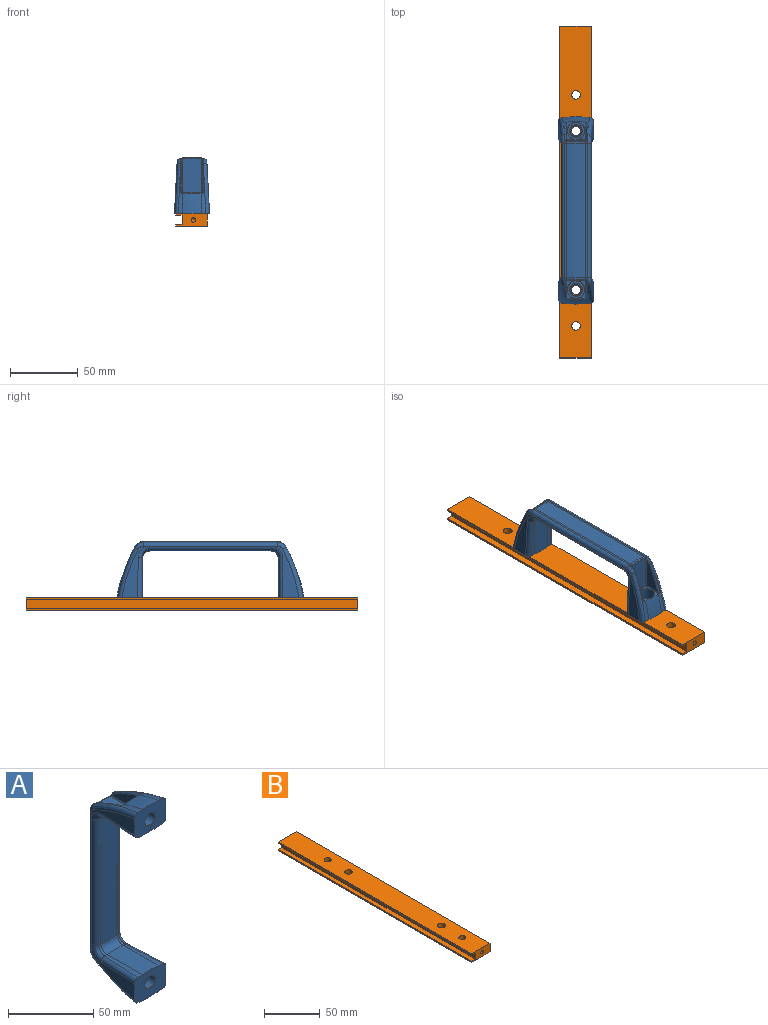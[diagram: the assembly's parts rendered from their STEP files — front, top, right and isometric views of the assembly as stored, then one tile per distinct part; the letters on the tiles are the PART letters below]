
ASSEMBLY  parts=2 mates=1
PART A: 126 faces, bbox 108.4x66.4x148.5 mm
  f0: bspline ~10.41x1.42mm, area 0.9mm2, adj f1,f4,f12,f108,f116
  f1: bspline ~20.12x1.18mm, area 9.2mm2, adj f0,f2,f15,f108
  f2: bspline ~9.59x1.35mm, area 0.9mm2, adj f1,f3,f13,f108,f112
  f3: bspline ~1.58x0.7mm, area 0.1mm2, adj f2,f53,f111
  f4: bspline ~1.56x0.73mm, area 0.1mm2, adj f0,f61,f113
  f5: bspline ~12.79x7.19mm, area 9.4mm2, adj f6,f7,f52,f110
  f6: torus R=125.24mm, axis (1,0,0), area 29.9mm2, adj f5,f14,f110,f115
  f7: bspline ~7.07x5.88mm, area 9.7mm2, adj f5,f53,f110,f111,f112,f114
  f8: bspline ~12.79x7.19mm, area 9.4mm2, adj f9,f10,f60,f107
  f9: torus R=125.24mm, axis (-1,0,0), area 29.9mm2, adj f8,f11,f107,f125
  f10: bspline ~7.07x5.88mm, area 9.7mm2, adj f8,f61,f107,f113,f116,f119
  f11: cone r=127mm half-angle=5deg, axis (-1,0,0), area 57.6mm2, adj f9,f29,f60,f75,f109,f125
  f12: cone r=7.92mm half-angle=5deg, axis (-1,0,0), area 2.4mm2, adj f0,f15,f41,f61
  f13: cone r=7.92mm half-angle=5deg, axis (1,0,0), area 2.4mm2, adj f2,f15,f46,f53
  f14: cone r=127mm half-angle=5deg, axis (1,0,0), area 57.6mm2, adj f6,f29,f52,f75,f109,f115
  f15: revolved ~13.28x1.56mm, area 20.6mm2, adj f1,f12,f13,f74
  f16: bspline ~10.41x1.42mm, area 0.9mm2, adj f17,f20,f45,f83,f87
  f17: bspline ~20.12x1.18mm, area 9.2mm2, adj f16,f18,f73,f83
  f18: bspline ~9.59x1.35mm, area 0.9mm2, adj f17,f19,f42,f83,f93
  f19: bspline ~1.56x0.73mm, area 0.1mm2, adj f18,f58,f90
  f20: bspline ~1.58x0.7mm, area 0.1mm2, adj f16,f55,f86
  f21: bspline ~12.79x7.19mm, area 9.4mm2, adj f22,f23,f57,f82
  f22: bspline ~7.07x5.88mm, area 9.7mm2, adj f21,f58,f82,f90,f93,f95
  f23: torus R=125.24mm, axis (1,0,0), area 29.9mm2, adj f21,f43,f82,f100
  f24: bspline ~12.79x7.19mm, area 9.4mm2, adj f25,f26,f56,f85
  f25: torus R=125.24mm, axis (-1,0,0), area 29.9mm2, adj f24,f44,f85,f88
  f26: bspline ~7.07x5.88mm, area 9.7mm2, adj f24,f55,f85,f86,f87,f89
  f27: plane 130.63x37.88mm, normal (1,0.05,0), area 541.9mm2, adj f28,f29,f57,f58,f59,f60,f61,f62
  f28: plane 26.01x19.26mm, normal (0,-1,0), area 410.5mm2, adj f27,f30,f31,f36,f43,f44,f47,f56
  f29: plane 26.01x19.26mm, normal (0,-1,0), area 410.5mm2, adj f11,f14,f27,f30,f34,f37,f51,f52
  f30: plane 130.63x37.88mm, normal (-1,0.05,0), area 541.9mm2, adj f28,f29,f47,f48,f49,f50,f51,f52
  f31: plane 29.17x3.53mm, normal (-0.09,0,-1), area 80.9mm2, adj f28,f35,f47,f71
  f32: plane 89.92x1.56mm, normal (-0.09,-1,0), area 140.9mm2, adj f33,f35,f49,f69
  f33: cone r=4.57mm half-angle=5deg, axis (-1,0,0), area 14.7mm2, adj f32,f34,f50,f68
  f34: plane 29.17x3.53mm, normal (-0.09,0,1), area 80.9mm2, adj f29,f33,f51,f67
  f35: cone r=4.57mm half-angle=5deg, axis (-1,0,0), area 14.7mm2, adj f31,f32,f48,f70
  f36: plane 29.17x3.53mm, normal (0.09,0,-1), area 80.9mm2, adj f28,f40,f62,f71
  f37: plane 29.17x3.53mm, normal (0.09,0,1), area 80.9mm2, adj f29,f38,f64,f67
  f38: cone r=4.57mm half-angle=5deg, axis (1,0,0), area 14.7mm2, adj f37,f39,f66,f68
  f39: plane 89.92x1.56mm, normal (0.09,-1,0), area 140.9mm2, adj f38,f40,f65,f69
  f40: cone r=4.57mm half-angle=5deg, axis (1,0,0), area 14.7mm2, adj f36,f39,f63,f70
  f41: plane 99.06x1.55mm, normal (0.09,1,0), area 154.1mm2, adj f12,f42,f59,f74
  f42: cone r=7.92mm half-angle=5deg, axis (-1,0,0), area 2.4mm2, adj f18,f41,f58,f73
  f43: cone r=127mm half-angle=5deg, axis (-1,0,0), area 57.6mm2, adj f23,f28,f57,f72,f84,f100
  f44: cone r=127mm half-angle=5deg, axis (1,0,0), area 57.6mm2, adj f25,f28,f56,f72,f84,f88
  f45: cone r=7.92mm half-angle=5deg, axis (1,0,0), area 2.4mm2, adj f16,f46,f55,f73
  f46: plane 99.06x1.55mm, normal (-0.09,1,0), area 154.1mm2, adj f13,f45,f54,f74
  f47: cylinder r=3.05mm len=29.49mm, axis (0.05,1,0), area 132.5mm2, adj f28,f30,f31,f48
  f48: bspline ~8.49x8.36mm, area 46.8mm2, adj f30,f35,f47,f49
  f49: cylinder r=3.05mm len=89.92mm, axis (0,0,-1), area 420.9mm2, adj f30,f32,f48,f50
  f50: bspline ~8.49x8.36mm, area 46.8mm2, adj f30,f33,f49,f51
  f51: cylinder r=3.05mm len=29.49mm, axis (-0.05,-1,0), area 132.5mm2, adj f29,f30,f34,f50
  f52: bspline ~51.85x20.13mm, area 172mm2, adj f5,f14,f29,f30,f53
  f53: bspline ~6.76x5.61mm, area 25.8mm2, adj f3,f7,f13,f30,f52,f54
  f54: cylinder r=3.05mm len=99.06mm, axis (0,0,1), area 432.1mm2, adj f30,f46,f53,f55
  f55: bspline ~6.76x5.61mm, area 25.8mm2, adj f20,f26,f30,f45,f54,f56
  f56: bspline ~51.85x20.13mm, area 172mm2, adj f24,f28,f30,f44,f55
  f57: bspline ~51.85x20.13mm, area 172mm2, adj f21,f27,f28,f43,f58
  f58: bspline ~6.76x5.61mm, area 25.8mm2, adj f19,f22,f27,f42,f57,f59
  f59: cylinder r=3.05mm len=99.06mm, axis (0,0,1), area 432.1mm2, adj f27,f41,f58,f61
  f60: bspline ~51.85x20.13mm, area 172mm2, adj f8,f11,f27,f29,f61
  f61: bspline ~6.76x5.61mm, area 25.8mm2, adj f4,f10,f12,f27,f59,f60
  f62: cylinder r=3.05mm len=29.49mm, axis (-0.05,1,0), area 132.5mm2, adj f27,f28,f36,f63
  f63: bspline ~8.49x8.36mm, area 46.8mm2, adj f27,f40,f62,f65
  f64: cylinder r=3.05mm len=29.49mm, axis (0.05,-1,0), area 132.5mm2, adj f27,f29,f37,f66
  f65: cylinder r=3.05mm len=89.92mm, axis (0,0,-1), area 420.9mm2, adj f27,f39,f63,f66
  f66: bspline ~8.49x8.36mm, area 46.8mm2, adj f27,f38,f64,f65
  f67: cylinder r=76.2mm len=29.17mm, axis (0,-1,0), area 388mm2, adj f29,f34,f37,f68
  f68: torus R=81.06mm, axis (1,0,0), area 103.6mm2, adj f33,f38,f67,f69
  f69: cylinder r=76.2mm len=89.92mm, axis (0,0,-1), area 1195.8mm2, adj f32,f39,f68,f70
  f70: torus R=81.06mm, axis (1,0,0), area 103.6mm2, adj f35,f40,f69,f71
  f71: cylinder r=76.2mm len=29.17mm, axis (0,1,0), area 388mm2, adj f28,f31,f36,f70
  f72: torus R=50.51mm, axis (-1,0,0), area 205.4mm2, adj f28,f43,f44,f84
  f73: revolved ~13.28x1.56mm, area 20.6mm2, adj f17,f42,f45,f74
  f74: cylinder r=76.2mm len=99.06mm, axis (0,0,1), area 1317.4mm2, adj f15,f41,f46,f73
  f75: torus R=50.51mm, axis (-1,0,0), area 205.4mm2, adj f11,f14,f29,f109
  f76: cone r=4.46mm half-angle=45deg, axis (0,-1,0), area 9.8mm2, adj f28,f77
  f77: cylinder r=4.2mm len=8.41mm, axis (0,-1,0), area 140.9mm2, adj f76,f78
  f78: cone r=4.2mm half-angle=45deg, axis (0,1,0), area 20.1mm2, adj f77,f79
  f79: plane 12.57x12.57mm, normal (0,1,0), area 54.4mm2, adj f78,f80
  f80: cone r=6.29mm half-angle=45deg, axis (0,1,0), area 14.5mm2, adj f79,f81
  f81: cylinder r=6.54mm len=13.08mm, axis (0,-1,0), area 354.9mm2, adj f80,f84
  f82: plane 23.7x11.76mm, normal (-1,0,0), area 167.7mm2, adj f21,f22,f23,f97,f99
  f83: plane 25.05x14.51mm, normal (0,0,1), area 346.4mm2, adj f16,f17,f18,f89,f92,f95,f96,f97
  f84: plane 15.37x13.63mm, normal (0,1,0), area 51.3mm2, adj f43,f44,f72,f81,f88,f91,f96,f99
  f85: plane 23.7x11.76mm, normal (1,0,0), area 167.7mm2, adj f24,f25,f26,f91,f92
  f86: bspline ~0.86x0.54mm, area 0mm2, adj f20,f26,f87
  f87: bspline ~1.16x0.66mm, area 0.4mm2, adj f16,f26,f86,f89
  f88: bspline ~1.97x1.77mm, area 1.2mm2, adj f25,f44,f84,f91
  f89: bspline ~1.66x0.87mm, area 0.6mm2, adj f26,f83,f87,f92
  f90: bspline ~0.86x0.54mm, area 0mm2, adj f19,f22,f93
  f91: cylinder r=0.51mm len=11.75mm, axis (0,0,1), area 9.4mm2, adj f84,f85,f88,f94
  f92: cylinder r=0.51mm len=23.7mm, axis (0,1,0), area 18.9mm2, adj f83,f85,f89,f94
  f93: bspline ~1.18x0.75mm, area 0.4mm2, adj f18,f22,f90,f95
  f94: sphere r=0.51mm, area 0.4mm2, adj f91,f92,f96
  f95: bspline ~1.36x0.87mm, area 0.6mm2, adj f22,f83,f93,f97
  f96: cylinder r=0.51mm len=13.88mm, axis (-1,0,0), area 11.1mm2, adj f83,f84,f94,f98
  f97: cylinder r=0.51mm len=23.7mm, axis (0,1,0), area 18.9mm2, adj f82,f83,f95,f98
  f98: sphere r=0.51mm, area 0.4mm2, adj f96,f97,f99
  f99: cylinder r=0.51mm len=11.75mm, axis (0,0,-1), area 9.4mm2, adj f82,f84,f98,f100
  f100: bspline ~1.99x1.84mm, area 1.2mm2, adj f23,f43,f84,f99
  f101: cone r=4.46mm half-angle=45deg, axis (0,-1,0), area 9.8mm2, adj f29,f102
  f102: cylinder r=4.2mm len=8.41mm, axis (0,-1,0), area 140.9mm2, adj f101,f103
  f103: cone r=4.2mm half-angle=45deg, axis (0,1,0), area 20.1mm2, adj f102,f104
  f104: plane 12.57x12.57mm, normal (0,1,0), area 54.4mm2, adj f103,f105
  f105: cone r=6.29mm half-angle=45deg, axis (0,1,0), area 14.5mm2, adj f104,f106
  f106: cylinder r=6.54mm len=13.08mm, axis (0,-1,0), area 354.9mm2, adj f105,f109
  f107: plane 23.7x11.76mm, normal (-1,0,0), area 167.7mm2, adj f8,f9,f10,f121,f124
  f108: plane 25.05x14.51mm, normal (0,0,-1), area 346.4mm2, adj f0,f1,f2,f114,f117,f119,f121,f122
  f109: plane 15.37x13.63mm, normal (0,1,0), area 51.3mm2, adj f11,f14,f75,f106,f115,f118,f122,f124
  f110: plane 23.7x11.76mm, normal (1,0,0), area 167.7mm2, adj f5,f6,f7,f117,f118
  f111: bspline ~0.86x0.54mm, area 0mm2, adj f3,f7,f112
  f112: bspline ~1.18x0.75mm, area 0.4mm2, adj f2,f7,f111,f114
  f113: bspline ~0.86x0.54mm, area 0mm2, adj f4,f10,f116
  f114: bspline ~1.66x0.87mm, area 0.6mm2, adj f7,f108,f112,f117
  f115: bspline ~1.99x1.84mm, area 1.2mm2, adj f6,f14,f109,f118
  f116: bspline ~1.16x0.66mm, area 0.4mm2, adj f0,f10,f113,f119
  f117: cylinder r=0.51mm len=23.7mm, axis (0,1,0), area 18.9mm2, adj f108,f110,f114,f120
  f118: cylinder r=0.51mm len=11.75mm, axis (0,0,1), area 9.4mm2, adj f109,f110,f115,f120
  f119: bspline ~1.66x0.87mm, area 0.6mm2, adj f10,f108,f116,f121
  f120: sphere r=0.51mm, area 0.4mm2, adj f117,f118,f122
  f121: cylinder r=0.51mm len=23.7mm, axis (0,1,0), area 18.9mm2, adj f107,f108,f119,f123
  f122: cylinder r=0.51mm len=13.88mm, axis (1,0,0), area 11.1mm2, adj f108,f109,f120,f123
  f123: sphere r=0.51mm, area 0.4mm2, adj f121,f122,f124
  f124: cylinder r=0.51mm len=11.75mm, axis (0,0,-1), area 9.4mm2, adj f107,f109,f123,f125
  f125: bspline ~1.97x1.77mm, area 1.2mm2, adj f9,f11,f109,f124
PART B: 18 faces, bbox 23.1x244.6x9.5 mm
  f0: plane 244.6x1.42mm, normal (-1,0,0), area 347.9mm2, adj f1,f3,f5,f8
  f1: plane 23.11x9.53mm, normal (0,-1,0), area 181.1mm2, adj f0,f2,f4,f5,f6,f7,f8,f9
  f2: plane 244.6x9.53mm, normal (1,0,0), area 2329.8mm2, adj f1,f3,f5,f6
  f3: plane 23.11x9.53mm, normal (0,1,0), area 181.1mm2, adj f0,f2,f4,f5,f6,f7,f8,f9
  f4: plane 244.6x1.42mm, normal (-1,0,0), area 347.9mm2, adj f1,f3,f6,f7
  f5: plane 244.6x23.11mm, normal (0,0,1), area 5517.8mm2, adj f0,f1,f2,f3,f10,f11,f16,f17
  f6: plane 244.6x23.11mm, normal (0,0,-1), area 5517.8mm2, adj f1,f2,f3,f4,f10,f11,f16,f17
  f7: plane 244.6x4.57mm, normal (0,0,1), area 1118.3mm2, adj f1,f3,f4,f9
  f8: plane 244.6x4.57mm, normal (0,0,-1), area 1118.3mm2, adj f0,f1,f3,f9
  f9: plane 244.6x6.68mm, normal (-1,0,0), area 1634mm2, adj f1,f3,f7,f8
  f10: cylinder r=3.17mm len=9.53mm, axis (0,0,1), area 190mm2, adj f5,f6
  f11: cylinder r=3.17mm len=9.53mm, axis (0,0,1), area 190mm2, adj f5,f6
  f12: cylinder r=1.65mm len=10.16mm, axis (0,1,0), area 105.3mm2, adj f3,f13
  f13: cone r=0mm half-angle=59deg, axis (0,1,0), area 10mm2, adj f12
  f14: cylinder r=1.65mm len=10.16mm, axis (0,-1,0), area 105.3mm2, adj f1,f15
  f15: cone r=0mm half-angle=59deg, axis (0,-1,0), area 10mm2, adj f14
  f16: cylinder r=3.4mm len=9.53mm, axis (0,0,1), area 203.5mm2, adj f5,f6
  f17: cylinder r=3.4mm len=9.53mm, axis (0,0,1), area 203.5mm2, adj f5,f6
PLACE A rot(axis=(0,0.71,0.71),180deg) t=(-8.94,-50.76,7.68)mm
PLACE B t=(2.24,-159.49,-0.71)mm
MATE fastened A.f101 <-> B.f17  axis (0,0,-1) through (-8.94,-109.31,8.81)mm
